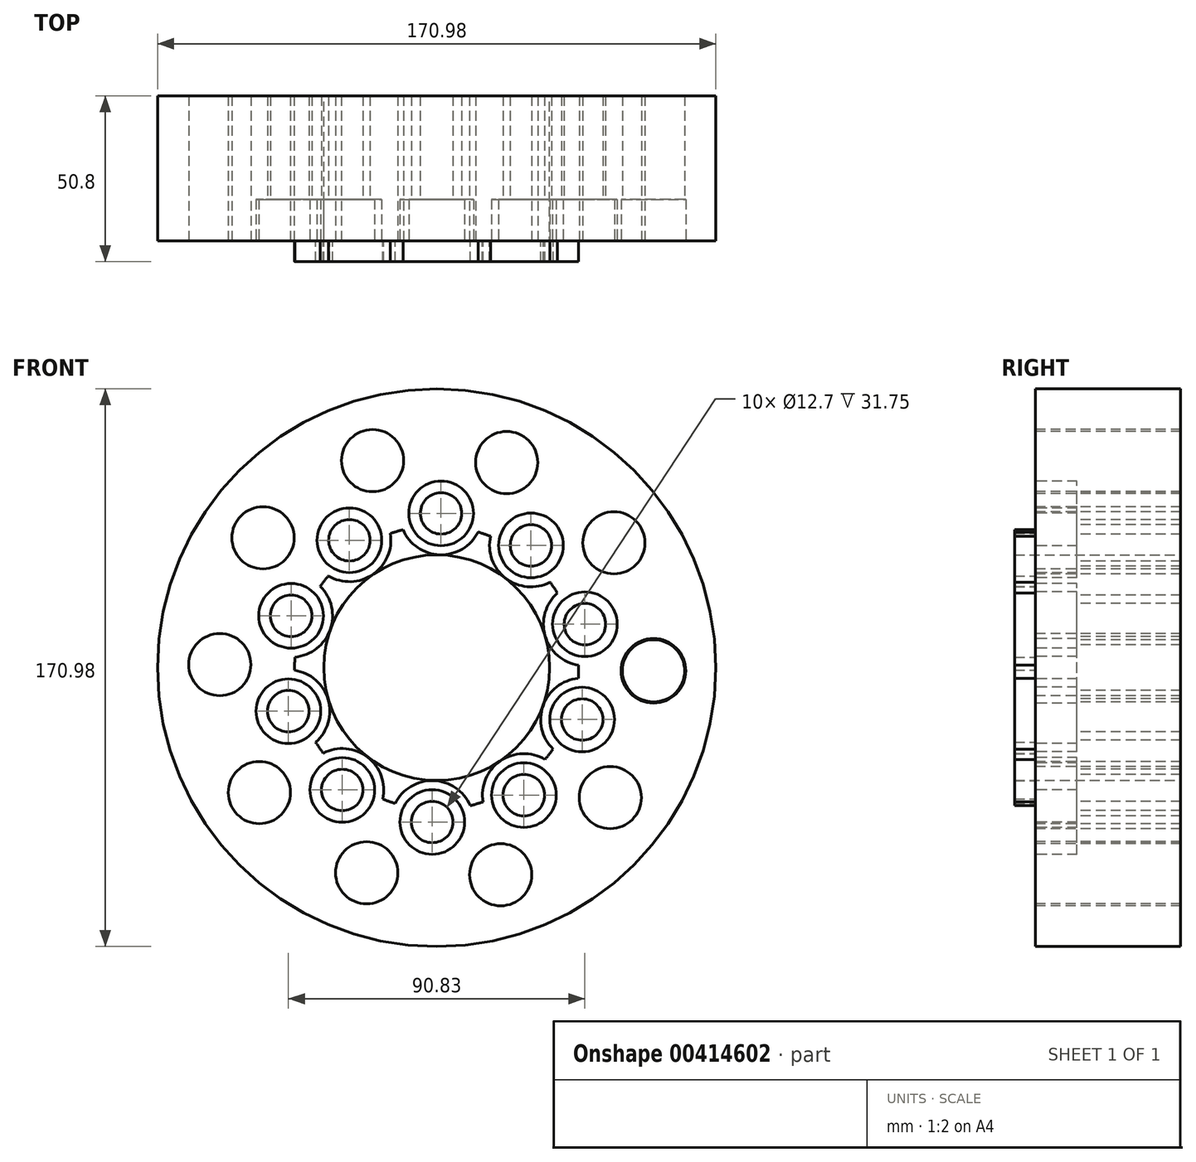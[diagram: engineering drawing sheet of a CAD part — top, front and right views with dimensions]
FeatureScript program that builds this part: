
annotation { "Feature Type Name" : "Feature", "Feature Type Description" : "" }
export const myFeature = defineFeature(function(context is Context, id is Id, definition is map)
    precondition{}
    {
        {
            var Q0;
            Q0=qCreatedBy(makeId("Front.planeOp"),FACE);
            var sketch = newSketch(context, id + "F0", { "sketchPlane" : qUnion([Q0])});
            skCircle(sketch, "E0", {"center": v(0, 0) * mm, "radius": 85.5 * mm});
            skCircle(sketch, "E1", {"center": v(0, 0) * mm, "radius": 43.5 * mm});
            skCircle(sketch, "E2", {"center": v(0, 0) * mm, "radius": 34.57 * mm});
            skSolve(sketch);
        }
        {
            var Q0;
            Q0=makeQuery(id+"F0.imprint","IMPRINT",FACE,{"disambiguationData":[TD([[makeQuery(id+"F0.imprint","IMPRINT",EDGE,{"derivedFrom":sQuery(id+"F0.wireOp",EDGE,"E1")}),1.0]])]});
            extrude(context, id + "F1", {"entities" : qUnion([Q0]), "depth" : 50.8 * mm});
        }
        {
            var Q0;
            Q0=makeQuery(id+"F0.imprint","IMPRINT",FACE,{"disambiguationData":[TD([[makeQuery(id+"F0.imprint","IMPRINT",EDGE,{"derivedFrom":sQuery(id+"F0.wireOp",EDGE,"E0")}),1.0]])]});
            extrude(context, id + "F2", {"entities" : qUnion([Q0]), "operationType" : NewBodyOperationType.ADD, "depth" : 44.45 * mm});
        }
        {
            var Q0;
            Q0=makeQuery(id+"F2.opExtrude","CAP_FACE",FACE,{"disambiguationData":[OSD([sQuery(id+"F0.wireOp",EDGE,"E0"),sQuery(id+"F0.wireOp",EDGE,"E1")])],"isStart":false});
            var sketch = newSketch(context, id + "F3", { "sketchPlane" : qUnion([Q0])});
            skSolve(sketch);
        }
        {
            var Q0;
            Q0=makeQuery(id+"F3.imprint","IMPRINT",FACE,{"disambiguationData":[TD([[makeQuery(id+"F3.imprint","IMPRINT",EDGE,{"derivedFrom":makeQuery(id+"F2.opExtrude","CAP_EDGE",EDGE,{"disambiguationData":[OSD([sQuery(id+"F0.wireOp",EDGE,"E0")])],"isStart":false})}),1.0]])]});
            var sketch = newSketch(context, id + "F4", { "sketchPlane" : qUnion([Q0])});
            skPoint(sketch, "E3", {"position": v(21.44, 62.88) * mm});
            skPoint(sketch, "E4.1.0", {"position": v(-19.62, 63.47) * mm});
            skPoint(sketch, "E4.2.0", {"position": v(-53.18, 39.82) * mm});
            skPoint(sketch, "E4.3.0", {"position": v(-66.43, 0.96) * mm});
            skPoint(sketch, "E4.4.0", {"position": v(-54.3, -38.27) * mm});
            skPoint(sketch, "E4.5.0", {"position": v(-21.44, -62.88) * mm});
            skPoint(sketch, "E4.6.0", {"position": v(19.62, -63.47) * mm});
            skPoint(sketch, "E4.7.0", {"position": v(53.18, -39.82) * mm});
            skPoint(sketch, "E4.8.0", {"position": v(66.43, -0.96) * mm});
            skPoint(sketch, "E4.9.0", {"position": v(54.3, 38.27) * mm});
            skPoint(sketch, "E4.center", {"position": v(0, 0) * mm});
            skSolve(sketch);
        }
        {
            var Q0;
            Q0=sQuery(id+"F4.wireOp",VERTEX,"E4.1.0");
            var Q1;
            Q1=makeQuery(id+"F1.opExtrude","SWEPT_BODY",BODY,{"disambiguationData":[OSD([sQuery(id+"F0.wireOp",EDGE,"E1"),sQuery(id+"F0.wireOp",EDGE,"E2")])]});
            hole(context, id + "F5", {"style" : HoleStyle.SIMPLE, "endStyle" : HoleEndStyle.THROUGH, "holeDiameter" : 6.35 * mm, "isTappedThrough" : true, "tappedDepth" : 12.7 * mm, "tapClearance" : 3, "locations" : qUnion([Q0]), "scope" : qUnion([Q1])});
        }
        {
            var Q0;
            Q0=sQuery(id+"F4.wireOp",VERTEX,"E4.2.0");
            var Q1;
            Q1=makeQuery(id+"F1.opExtrude","SWEPT_BODY",BODY,{"disambiguationData":[OSD([sQuery(id+"F0.wireOp",EDGE,"E1"),sQuery(id+"F0.wireOp",EDGE,"E2")])]});
            hole(context, id + "F6", {"style" : HoleStyle.SIMPLE, "endStyle" : HoleEndStyle.THROUGH, "holeDiameter" : 6.35 * mm, "isTappedThrough" : true, "tappedDepth" : 12.7 * mm, "tapClearance" : 3, "locations" : qUnion([Q0]), "scope" : qUnion([Q1])});
        }
        {
            var Q0;
            Q0=sQuery(id+"F4.wireOp",VERTEX,"E4.3.0");
            var Q1;
            Q1=sQuery(id+"F4.wireOp",VERTEX,"E4.4.0");
            var Q2;
            Q2=sQuery(id+"F4.wireOp",VERTEX,"E4.5.0");
            var Q3;
            Q3=sQuery(id+"F4.wireOp",VERTEX,"E4.6.0");
            var Q4;
            Q4=sQuery(id+"F4.wireOp",VERTEX,"E4.7.0");
            var Q5;
            Q5=sQuery(id+"F4.wireOp",VERTEX,"E4.8.0");
            var Q6;
            Q6=sQuery(id+"F4.wireOp",VERTEX,"E4.9.0");
            var Q7;
            Q7=sQuery(id+"F4.wireOp",VERTEX,"E3");
            var Q8;
            Q8=makeQuery(id+"F1.opExtrude","SWEPT_BODY",BODY,{"disambiguationData":[OSD([sQuery(id+"F0.wireOp",EDGE,"E1"),sQuery(id+"F0.wireOp",EDGE,"E2")])]});
            hole(context, id + "F7", {"style" : HoleStyle.SIMPLE, "endStyle" : HoleEndStyle.THROUGH, "holeDiameter" : 6.35 * mm, "isTappedThrough" : true, "tappedDepth" : 12.7 * mm, "tapClearance" : 3, "locations" : qUnion([Q0, Q1, Q2, Q3, Q4, Q5, Q6, Q7]), "scope" : qUnion([Q8])});
        }
        {
            var Q0;
            Q0=makeQuery(id+"F4.imprint","IMPRINT",FACE,{"disambiguationData":[TD([[makeQuery(id+"F4.imprint","IMPRINT",EDGE,{"derivedFrom":makeQuery(id+"F3.imprint","IMPRINT",EDGE,{"derivedFrom":makeQuery(id+"F2.opExtrude","CAP_EDGE",EDGE,{"disambiguationData":[OSD([sQuery(id+"F0.wireOp",EDGE,"E0")])],"isStart":false})})}),1.0]])]});
            var sketch = newSketch(context, id + "F8", { "sketchPlane" : qUnion([Q0])});
            skPoint(sketch, "E5", {"position": v(28.9, 37.48) * mm});
            skPoint(sketch, "E6.1.0", {"position": v(1.35, 47.31) * mm});
            skPoint(sketch, "E6.2.0", {"position": v(-26.72, 39.07) * mm});
            skPoint(sketch, "E6.3.0", {"position": v(-44.58, 15.9) * mm});
            skPoint(sketch, "E6.4.0", {"position": v(-45.41, -13.33) * mm});
            skPoint(sketch, "E6.5.0", {"position": v(-28.9, -37.48) * mm});
            skPoint(sketch, "E6.6.0", {"position": v(-1.35, -47.31) * mm});
            skPoint(sketch, "E6.7.0", {"position": v(26.72, -39.07) * mm});
            skPoint(sketch, "E6.8.0", {"position": v(44.58, -15.9) * mm});
            skPoint(sketch, "E6.9.0", {"position": v(45.41, 13.33) * mm});
            skPoint(sketch, "E6.center", {"position": v(0, 0) * mm});
            skSolve(sketch);
        }
        {
            var Q0;
            Q0=sQuery(id+"F8.wireOp",VERTEX,"E6.3.0");
            var Q1;
            Q1=sQuery(id+"F8.wireOp",VERTEX,"E6.4.0");
            var Q2;
            Q2=sQuery(id+"F8.wireOp",VERTEX,"E6.5.0");
            var Q3;
            Q3=sQuery(id+"F8.wireOp",VERTEX,"E6.6.0");
            var Q4;
            Q4=sQuery(id+"F8.wireOp",VERTEX,"E6.7.0");
            var Q5;
            Q5=sQuery(id+"F8.wireOp",VERTEX,"E6.8.0");
            var Q6;
            Q6=sQuery(id+"F8.wireOp",VERTEX,"E6.9.0");
            var Q7;
            Q7=sQuery(id+"F8.wireOp",VERTEX,"E5");
            var Q8;
            Q8=sQuery(id+"F8.wireOp",VERTEX,"E6.1.0");
            var Q9;
            Q9=sQuery(id+"F8.wireOp",VERTEX,"E6.2.0");
            var Q10;
            Q10=makeQuery(id+"F1.opExtrude","SWEPT_BODY",BODY,{"disambiguationData":[OSD([sQuery(id+"F0.wireOp",EDGE,"E1"),sQuery(id+"F0.wireOp",EDGE,"E2")])]});
            hole(context, id + "F9", {"style" : HoleStyle.C_BORE, "endStyle" : HoleEndStyle.THROUGH, "oppositeDirection" : true, "holeDiameter" : 12.7 * mm, "cBoreDiameter" : 25.4 * mm, "cBoreDepth" : 12.7 * mm, "isTappedThrough" : true, "tappedDepth" : 12.7 * mm, "tapClearance" : 3, "locations" : qUnion([Q0, Q1, Q2, Q3, Q4, Q5, Q6, Q7, Q8, Q9]), "scope" : qUnion([Q10])});
        }
        {
            var Q0;
            Q0=sQuery(id+"F8.wireOp",VERTEX,"E6.2.0");
            var Q1;
            Q1=sQuery(id+"F8.wireOp",VERTEX,"E6.1.0");
            var Q2;
            Q2=sQuery(id+"F8.wireOp",VERTEX,"E5");
            var Q3;
            Q3=sQuery(id+"F8.wireOp",VERTEX,"E6.9.0");
            var Q4;
            Q4=sQuery(id+"F8.wireOp",VERTEX,"E6.8.0");
            var Q5;
            Q5=sQuery(id+"F8.wireOp",VERTEX,"E6.7.0");
            var Q6;
            Q6=sQuery(id+"F8.wireOp",VERTEX,"E6.6.0");
            var Q7;
            Q7=sQuery(id+"F8.wireOp",VERTEX,"E6.5.0");
            var Q8;
            Q8=sQuery(id+"F8.wireOp",VERTEX,"E6.4.0");
            var Q9;
            Q9=sQuery(id+"F8.wireOp",VERTEX,"E6.3.0");
            var Q10;
            Q10=sQuery(id+"F4.wireOp",VERTEX,"E4.8.0");
            var Q11;
            Q11=makeQuery(id+"F1.opExtrude","SWEPT_BODY",BODY,{"disambiguationData":[OSD([sQuery(id+"F0.wireOp",EDGE,"E1"),sQuery(id+"F0.wireOp",EDGE,"E2")])]});
            hole(context, id + "F10", {"style" : HoleStyle.C_BORE, "endStyle" : HoleEndStyle.THROUGH, "holeDiameter" : 12.7 * mm, "cBoreDiameter" : 19.8 * mm, "cBoreDepth" : 12.7 * mm, "isTappedThrough" : true, "tappedDepth" : 12.7 * mm, "tapClearance" : 3, "locations" : qUnion([Q0, Q1, Q2, Q3, Q4, Q5, Q6, Q7, Q8, Q9, Q10]), "scope" : qUnion([Q11])});
        }
        {
            var Q0;
            Q0=qCreatedBy(makeId("Front.planeOp"),FACE);
            var sketch = newSketch(context, id + "F11", { "sketchPlane" : qUnion([Q0])});
            skSolve(sketch);
        }
        {
            var Q0;
            Q0=sQuery(id+"F4.wireOp",VERTEX,"E4.3.0");
            var Q1;
            Q1=sQuery(id+"F4.wireOp",VERTEX,"E4.2.0");
            var Q2;
            Q2=sQuery(id+"F4.wireOp",VERTEX,"E4.1.0");
            var Q3;
            Q3=sQuery(id+"F4.wireOp",VERTEX,"E3");
            var Q4;
            Q4=sQuery(id+"F4.wireOp",VERTEX,"E4.9.0");
            var Q5;
            Q5=sQuery(id+"F4.wireOp",VERTEX,"E4.8.0");
            var Q6;
            Q6=sQuery(id+"F4.wireOp",VERTEX,"E4.7.0");
            var Q7;
            Q7=sQuery(id+"F4.wireOp",VERTEX,"E4.6.0");
            var Q8;
            Q8=sQuery(id+"F4.wireOp",VERTEX,"E4.5.0");
            var Q9;
            Q9=sQuery(id+"F4.wireOp",VERTEX,"E4.4.0");
            var Q10;
            Q10=makeQuery(id+"F1.opExtrude","SWEPT_BODY",BODY,{"disambiguationData":[OSD([sQuery(id+"F0.wireOp",EDGE,"E1"),sQuery(id+"F0.wireOp",EDGE,"E2")])]});
            hole(context, id + "F12", {"style" : HoleStyle.SIMPLE, "endStyle" : HoleEndStyle.THROUGH, "holeDiameter" : 19.05 * mm, "isTappedThrough" : true, "tappedDepth" : 12.7 * mm, "tapClearance" : 3, "locations" : qUnion([Q0, Q1, Q2, Q3, Q4, Q5, Q6, Q7, Q8, Q9]), "scope" : qUnion([Q10])});
        }
    });
